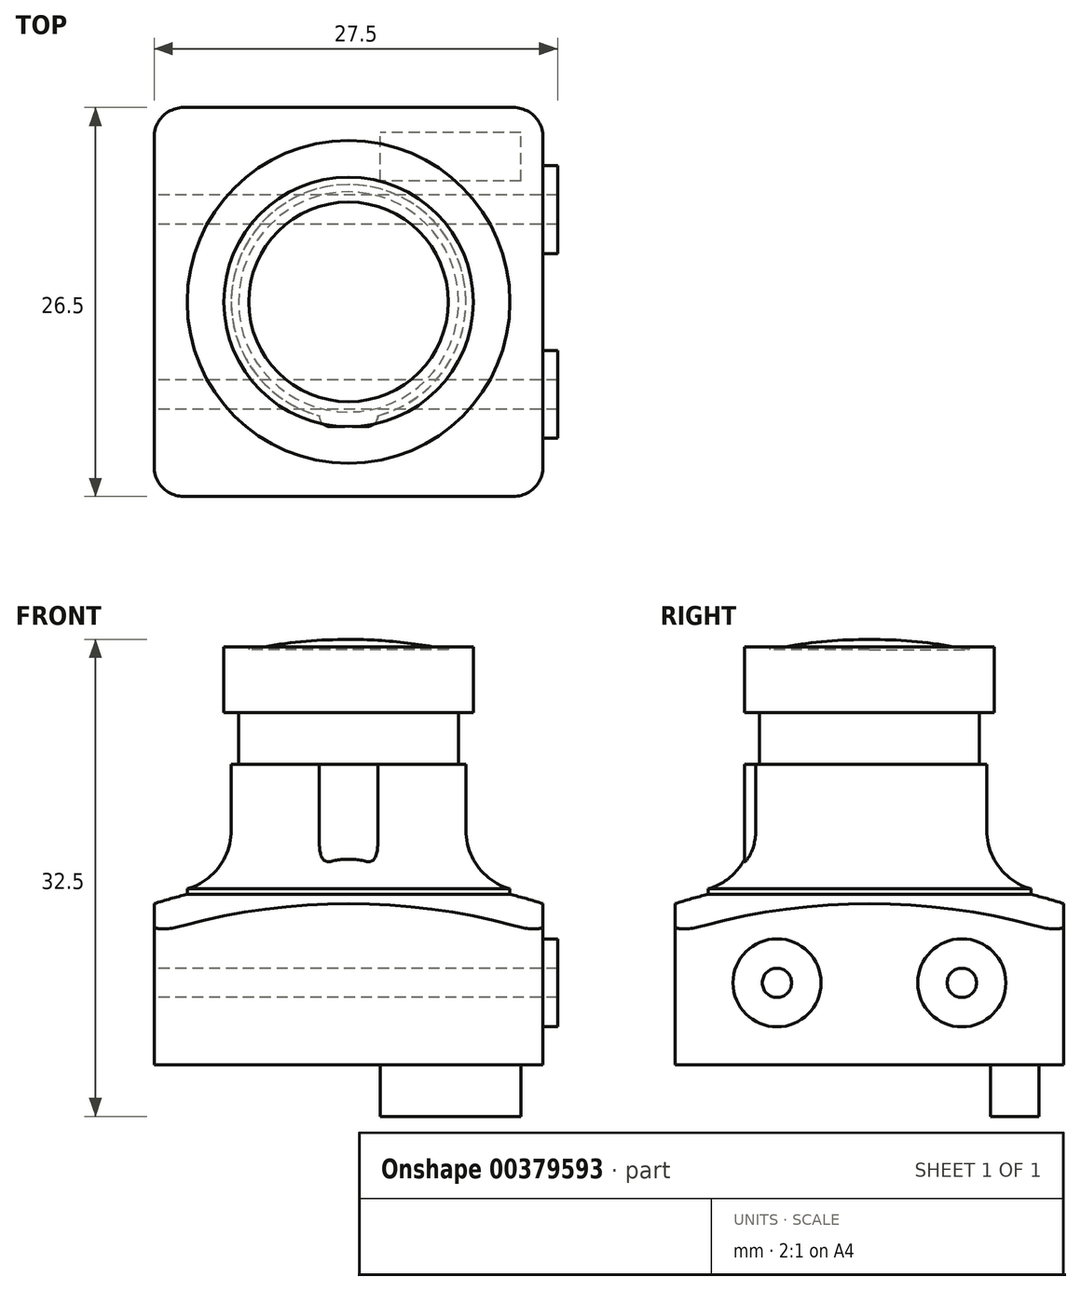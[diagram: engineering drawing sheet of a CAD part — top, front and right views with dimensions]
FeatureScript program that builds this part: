
annotation { "Feature Type Name" : "Feature", "Feature Type Description" : "" }
export const myFeature = defineFeature(function(context is Context, id is Id, definition is map)
    precondition{}
    {
        {
            var Q0;
            Q0=qCreatedBy(makeId("Top.planeOp"),FACE);
            var sketch = newSketch(context, id + "F0", { "sketchPlane" : qUnion([Q0])});
            skLineSegment(sketch, "E0.bottom", {"start": v(13.25, 13.25) * mm, "end": v(-13.25, 13.25) * mm});
            skLineSegment(sketch, "E0.top", {"start": v(13.25, -13.25) * mm, "end": v(-13.25, -13.25) * mm});
            skLineSegment(sketch, "E0.left", {"start": v(13.25, 13.25) * mm, "end": v(13.25, -13.25) * mm});
            skLineSegment(sketch, "E0.right", {"start": v(-13.25, 13.25) * mm, "end": v(-13.25, -13.25) * mm});
            skPoint(sketch, "E0.middle", {"position": v(0, 0) * mm});
            skSolve(sketch);
        }
        {
            var Q0;
            Q0 = qSketchRegion(id + "F0", true);
            extrude(context, id + "F1", {"entities" : qUnion([Q0]), "depth" : 25 * mm});
        }
        {
            var Q0;
            Q0=qCreatedBy(makeId("Front.planeOp"),FACE);
            var sketch = newSketch(context, id + "F2", { "sketchPlane" : qUnion([Q0])});
            skArc(sketch, "E1", {"start": v(23.25, 6.5) * mm, "mid": v(12.07, 11.35) * mm, "end": v(0, 13) * mm});
            skLineSegment(sketch, "E2", {"start": v(23.25, 6.5) * mm, "end": v(23.25, 25) * mm});
            skLineSegment(sketch, "E3", {"start": v(23.25, 25) * mm, "end": v(0, 25) * mm});
            skLineSegment(sketch, "E4", {"start": v(0, 25) * mm, "end": v(0, 13) * mm});
            skLineSegment(sketch, "E5", {"start": v(13.25, 25) * mm, "end": v(13.25, 11) * mm});
            skLineSegment(sketch, "E6", {"start": v(0, 13) * mm, "end": v(13.25, 13) * mm, "construction": true});
            skSolve(sketch);
        }
        {
            var Q0;
            Q0 = qSketchRegion(id + "F2", true);
            var Q1;
            Q1=sQuery(id+"F2.wireOp",EDGE,"E4");
            revolve(context, id + "F3", {"operationType" : NewBodyOperationType.REMOVE, "entities" : qUnion([Q0]), "axis" : qUnion([Q1]), "revolveType" : RevolveType.FULL, "oppositeDirection" : true});
        }
        {
            var Q0;
            Q0=makeQuery(id+"F1.opExtrude","SWEPT_FACE",FACE,{"disambiguationData":[OSD([sQuery(id+"F0.wireOp",EDGE,"E0.left")])]});
            var sketch = newSketch(context, id + "F4", { "sketchPlane" : qUnion([Q0])});
            skCircle(sketch, "E7", {"center": v(-6.3, 5.6) * mm, "radius": 3 * mm});
            skCircle(sketch, "E8", {"center": v(-6.3, 5.6) * mm, "radius": 1 * mm});
            skLineSegment(sketch, "E9", {"start": v(0, 0) * mm, "end": v(0, 11) * mm, "construction": true});
            skCircle(sketch, "E10.MirrorC", {"center": v(6.3, 5.6) * mm, "radius": 1 * mm});
            skCircle(sketch, "E11.MirrorC", {"center": v(6.3, 5.6) * mm, "radius": 3 * mm});
            skSolve(sketch);
        }
        {
            var Q0;
            Q0=qCreatedBy(makeId("Front.planeOp"),FACE);
            var sketch = newSketch(context, id + "F5", { "sketchPlane" : qUnion([Q0])});
            skLineSegment(sketch, "E12", {"start": v(0, 20.5) * mm, "end": v(0, 0) * mm});
            skLineSegment(sketch, "E13", {"start": v(0, 0) * mm, "end": v(11, 0) * mm});
            skLineSegment(sketch, "E14", {"start": v(11, 0) * mm, "end": v(11, 12) * mm});
            skLineSegment(sketch, "E15", {"start": v(0, 20.5) * mm, "end": v(8, 20.5) * mm});
            skLineSegment(sketch, "E16", {"start": v(8, 20.5) * mm, "end": v(8, 16) * mm});
            skArc(sketch, "E17", {"start": v(8, 16) * mm, "mid": v(8.83, 13.5) * mm, "end": v(11, 12) * mm});
            skSolve(sketch);
        }
        {
            var Q0;
            Q0 = qSketchRegion(id + "F5", true);
            var Q1;
            Q1=sQuery(id+"F5.wireOp",EDGE,"E12");
            revolve(context, id + "F6", {"operationType" : NewBodyOperationType.ADD, "entities" : qUnion([Q0]), "axis" : qUnion([Q1]), "revolveType" : RevolveType.FULL});
        }
        {
            var Q0;
            Q0=makeQuery(id+"F6.opRevolve","SWEPT_FACE",FACE,{"disambiguationData":[OSD([sQuery(id+"F5.wireOp",EDGE,"E15")])]});
            var sketch = newSketch(context, id + "F7", { "sketchPlane" : qUnion([Q0])});
            skCircle(sketch, "E18", {"center": v(0, 0) * mm, "radius": 7.5 * mm});
            skSolve(sketch);
        }
        {
            var Q0;
            Q0=makeQuery(id+"F7.imprint","IMPRINT",FACE,{"disambiguationData":[TD([[makeQuery(id+"F7.imprint","IMPRINT",EDGE,{"derivedFrom":sQuery(id+"F7.wireOp",EDGE,"E18")}),1.0]])]});
            extrude(context, id + "F8", {"entities" : qUnion([Q0]), "operationType" : NewBodyOperationType.ADD, "depth" : 3.5 * mm});
        }
        {
            var Q0;
            Q0=qCreatedBy(makeId("Front.planeOp"),FACE);
            var sketch = newSketch(context, id + "F9", { "sketchPlane" : qUnion([Q0])});
            skLineSegment(sketch, "E19", {"start": v(0, 24) * mm, "end": v(0, 29) * mm});
            skLineSegment(sketch, "E20", {"start": v(0, 24) * mm, "end": v(-8.5, 24) * mm});
            skLineSegment(sketch, "E21", {"start": v(-8.5, 24) * mm, "end": v(-8.5, 28.5) * mm});
            skLineSegment(sketch, "E22", {"start": v(-8.5, 28.5) * mm, "end": v(-6.8, 28.5) * mm});
            skLineSegment(sketch, "E23", {"start": v(-6.8, 28.5) * mm, "end": v(-6.8, 28.3) * mm});
            skLineSegment(sketch, "E24", {"start": v(0, 29) * mm, "end": v(-8.5, 29) * mm, "construction": true});
            skArc(sketch, "E25", {"start": v(0, 29) * mm, "mid": v(-3.42, 28.82) * mm, "end": v(-6.8, 28.3) * mm});
            skSolve(sketch);
        }
        {
            var Q0;
            Q0 = qSketchRegion(id + "F9", true);
            var Q1;
            Q1=sQuery(id+"F9.wireOp",EDGE,"E19");
            revolve(context, id + "F10", {"operationType" : NewBodyOperationType.ADD, "entities" : qUnion([Q0]), "axis" : qUnion([Q1]), "revolveType" : RevolveType.FULL});
        }
        {
            var Q0;
            Q0=makeQuery(id+"F6.opRevolve","SWEPT_FACE",FACE,{"disambiguationData":[OSD([sQuery(id+"F5.wireOp",EDGE,"E15")])]});
            var sketch = newSketch(context, id + "F11", { "sketchPlane" : qUnion([Q0])});
            skLineSegment(sketch, "E26", {"start": v(-2, -7.75) * mm, "end": v(-2, -8.5) * mm});
            skLineSegment(sketch, "E27", {"start": v(-2, -8.5) * mm, "end": v(2, -8.5) * mm});
            skLineSegment(sketch, "E28", {"start": v(2, -8.5) * mm, "end": v(2, -7.75) * mm});
            skArc(sketch, "E29", {"start": v(-2, -7.75) * mm, "mid": v(0, -8) * mm, "end": v(2, -7.75) * mm});
            skLineSegment(sketch, "E30", {"start": v(0, 0) * mm, "end": v(0, -8.5) * mm, "construction": true});
            skSolve(sketch);
        }
        {
            var Q0;
            Q0 = qSketchRegion(id + "F11", true);
            extrude(context, id + "F12", {"entities" : qUnion([Q0]), "operationType" : NewBodyOperationType.ADD, "endBound" : BoundingType.UP_TO_NEXT, "oppositeDirection" : true, "depth" : 25 * mm});
        }
        {
            var Q0;
            {var subQ0=sQuery(id+"F11.wireOp",EDGE,"E27");var subQ1=sQuery(id+"F11.wireOp",EDGE,"E28");Q0=makeQuery(id+"F12.boolean.opBoolean","SPLIT",EDGE,{"disambiguationData":[TD([makeQuery(id+"F6.opRevolve","SWEPT_FACE",FACE,{"disambiguationData":[OSD([sQuery(id+"F5.wireOp",EDGE,"E15")])]})])],"derivedFrom":makeQuery(id+"F12.opExtrude","SWEPT_EDGE",EDGE,{"disambiguationData":[OSD([subQ0,subQ1])]})});}
            var Q1;
            {var subQ0=sQuery(id+"F11.wireOp",EDGE,"E27");var subQ1=sQuery(id+"F11.wireOp",EDGE,"E26");Q1=makeQuery(id+"F12.boolean.opBoolean","SPLIT",EDGE,{"disambiguationData":[TD([makeQuery(id+"F6.opRevolve","SWEPT_FACE",FACE,{"disambiguationData":[OSD([sQuery(id+"F5.wireOp",EDGE,"E15")])]})])],"derivedFrom":makeQuery(id+"F12.opExtrude","SWEPT_EDGE",EDGE,{"disambiguationData":[OSD([subQ1,subQ0])]})});}
            fillet(context, id + "F13", {"entities" : qUnion([Q0, Q1]), "radius" : 0.75 * mm, "tangentPropagation" : true, "allowEdgeOverflow" : false});
        }
        {
            var Q0;
            Q0=makeQuery(id+"F1.opExtrude","CAP_FACE",FACE,{"disambiguationData":[OSD([sQuery(id+"F0.wireOp",EDGE,"E0.bottom"),sQuery(id+"F0.wireOp",EDGE,"E0.top"),sQuery(id+"F0.wireOp",EDGE,"E0.left"),sQuery(id+"F0.wireOp",EDGE,"E0.right")])],"isStart":true});
            var sketch = newSketch(context, id + "F14", { "sketchPlane" : qUnion([Q0])});
            skLineSegment(sketch, "E31.bottom", {"start": v(11.75, -8.25) * mm, "end": v(2.15, -8.25) * mm});
            skLineSegment(sketch, "E31.top", {"start": v(11.75, -11.55) * mm, "end": v(2.15, -11.55) * mm});
            skLineSegment(sketch, "E31.left", {"start": v(11.75, -8.25) * mm, "end": v(11.75, -11.55) * mm});
            skLineSegment(sketch, "E31.right", {"start": v(2.15, -8.25) * mm, "end": v(2.15, -11.55) * mm});
            skPoint(sketch, "E31.middle", {"position": v(6.95, -9.9) * mm});
            skSolve(sketch);
        }
        {
            var Q0;
            Q0 = qSketchRegion(id + "F14", true);
            extrude(context, id + "F15", {"entities" : qUnion([Q0]), "operationType" : NewBodyOperationType.ADD, "depth" : 3.5 * mm});
        }
        {
            var Q0;
            Q0 = qSketchRegion(id + "F4", true);
            extrude(context, id + "F16", {"entities" : qUnion([Q0]), "operationType" : NewBodyOperationType.ADD, "depth" : 1 * mm});
        }
        {
            var Q0;
            Q0=makeQuery(id+"F16.boolean.opBoolean","SPLIT",FACE,{"disambiguationData":[TD([makeQuery(id+"F16.opExtrude","SWEPT_FACE",FACE,{"disambiguationData":[OSD([sQuery(id+"F4.wireOp",EDGE,"E8")])]})])],"derivedFrom":makeQuery(id+"F1.opExtrude","SWEPT_FACE",FACE,{"disambiguationData":[OSD([sQuery(id+"F0.wireOp",EDGE,"E0.left")])]})});
            var Q1;
            Q1=makeQuery(id+"F16.boolean.opBoolean","SPLIT",FACE,{"disambiguationData":[TD([makeQuery(id+"F16.opExtrude","SWEPT_FACE",FACE,{"disambiguationData":[OSD([sQuery(id+"F4.wireOp",EDGE,"E10.MirrorC")])]})])],"derivedFrom":makeQuery(id+"F1.opExtrude","SWEPT_FACE",FACE,{"disambiguationData":[OSD([sQuery(id+"F0.wireOp",EDGE,"E0.left")])]})});
            extrude(context, id + "F17", {"entities" : qUnion([Q0, Q1]), "operationType" : NewBodyOperationType.REMOVE, "endBound" : BoundingType.THROUGH_ALL, "oppositeDirection" : true, "depth" : 25 * mm});
        }
        {
            var Q0;
            Q0=makeQuery(id+"F1.opExtrude","SWEPT_EDGE",EDGE,{"disambiguationData":[OSD([sQuery(id+"F0.wireOp",EDGE,"E0.top"),sQuery(id+"F0.wireOp",EDGE,"E0.right")])]});
            var Q1;
            Q1=makeQuery(id+"F1.opExtrude","SWEPT_EDGE",EDGE,{"disambiguationData":[OSD([sQuery(id+"F0.wireOp",EDGE,"E0.bottom"),sQuery(id+"F0.wireOp",EDGE,"E0.right")])]});
            var Q2;
            Q2=makeQuery(id+"F1.opExtrude","SWEPT_EDGE",EDGE,{"disambiguationData":[OSD([sQuery(id+"F0.wireOp",EDGE,"E0.top"),sQuery(id+"F0.wireOp",EDGE,"E0.left")])]});
            var Q3;
            Q3=makeQuery(id+"F1.opExtrude","SWEPT_EDGE",EDGE,{"disambiguationData":[OSD([sQuery(id+"F0.wireOp",EDGE,"E0.bottom"),sQuery(id+"F0.wireOp",EDGE,"E0.left")])]});
            fillet(context, id + "F18", {"entities" : qUnion([Q0, Q1, Q2, Q3]), "radius" : 2 * mm, "tangentPropagation" : true, "allowEdgeOverflow" : false});
        }
    });
